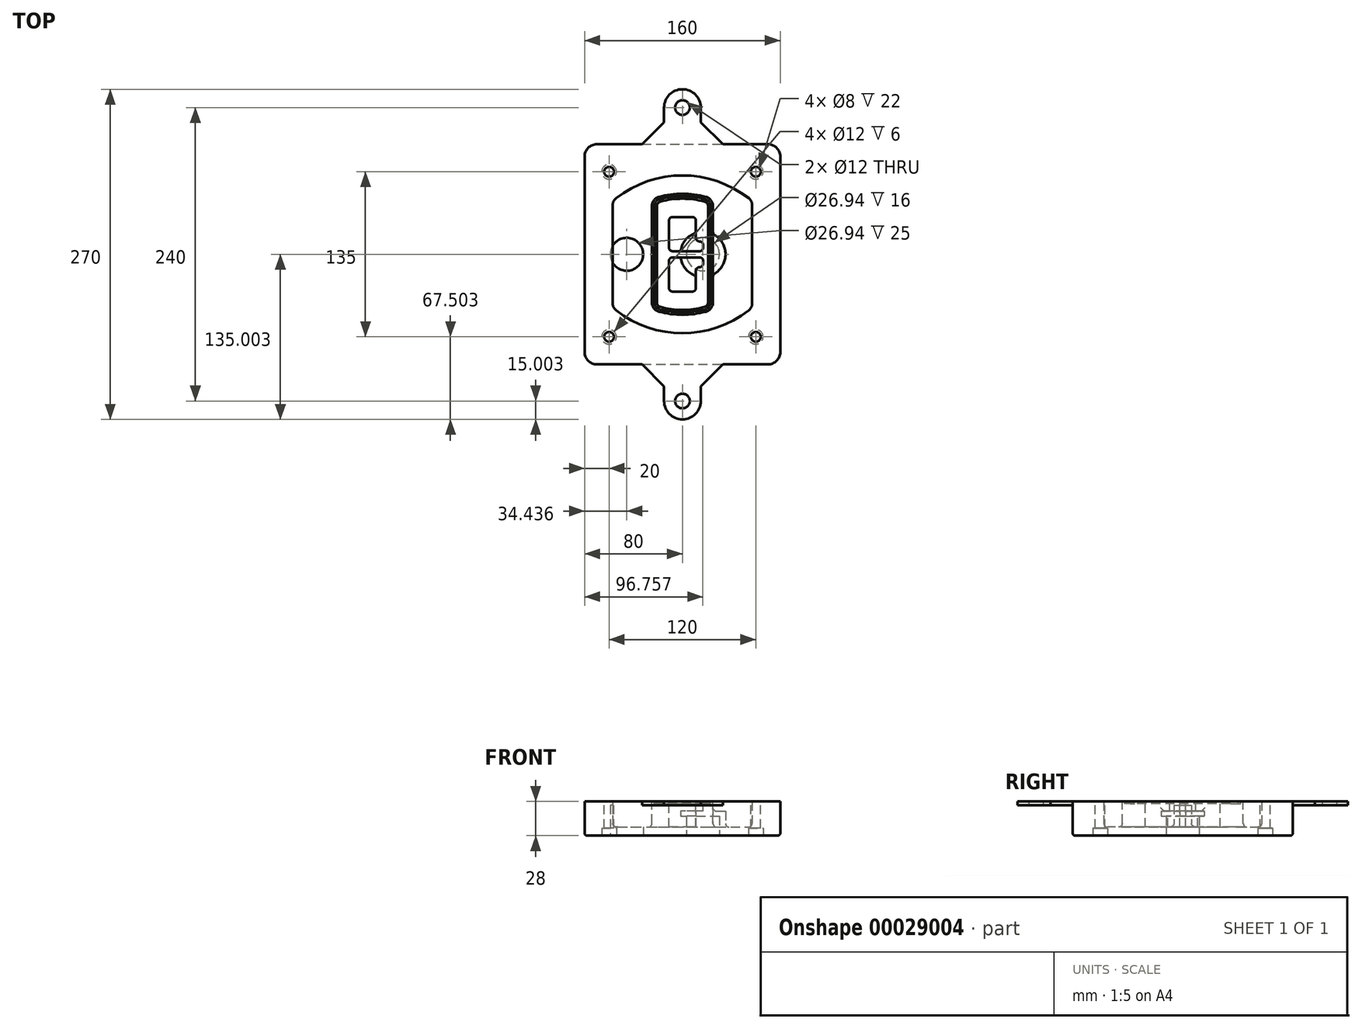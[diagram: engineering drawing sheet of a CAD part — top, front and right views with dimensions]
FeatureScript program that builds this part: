
annotation { "Feature Type Name" : "Feature", "Feature Type Description" : "" }
export const myFeature = defineFeature(function(context is Context, id is Id, definition is map)
    precondition{}
    {
        {
            var Q0;
            Q0=qCreatedBy(makeId("Top.planeOp"),FACE);
            var sketch = newSketch(context, id + "F0", { "sketchPlane" : qUnion([Q0])});
            skPoint(sketch, "E0.rect.middle", {"position": v(0, 0) * mm});
            skLineSegment(sketch, "E1.bottom", {"start": v(24.05, 28.38) * mm, "end": v(164.05, 28.38) * mm});
            skLineSegment(sketch, "E1.top", {"start": v(24.05, 208.38) * mm, "end": v(164.05, 208.38) * mm});
            skLineSegment(sketch, "E1.left", {"start": v(14.05, 38.38) * mm, "end": v(14.05, 198.38) * mm});
            skLineSegment(sketch, "E1.right", {"start": v(174.05, 38.38) * mm, "end": v(174.05, 198.38) * mm});
            skLineSegment(sketch, "E2", {"start": v(14.05, 208.38) * mm, "end": v(174.05, 28.38) * mm, "construction": true});
            skLineSegment(sketch, "E3", {"start": v(174.05, 208.38) * mm, "end": v(14.05, 28.38) * mm, "construction": true});
            skCircle(sketch, "E4", {"center": v(34.05, 185.88) * mm, "radius": 4 * mm});
            skCircle(sketch, "E5", {"center": v(154.05, 185.88) * mm, "radius": 4 * mm});
            skCircle(sketch, "E6", {"center": v(154.05, 50.88) * mm, "radius": 4 * mm});
            skCircle(sketch, "E7", {"center": v(34.05, 50.88) * mm, "radius": 4 * mm});
            skLineSegment(sketch, "E8", {"start": v(34.05, 185.88) * mm, "end": v(154.05, 185.88) * mm, "construction": true});
            skLineSegment(sketch, "E9", {"start": v(154.05, 185.88) * mm, "end": v(154.05, 50.88) * mm, "construction": true});
            skLineSegment(sketch, "E10", {"start": v(154.05, 50.88) * mm, "end": v(34.05, 50.88) * mm, "construction": true});
            skLineSegment(sketch, "E11", {"start": v(34.05, 50.88) * mm, "end": v(34.05, 185.88) * mm, "construction": true});
            skLineSegment(sketch, "E12", {"start": v(34.05, 158.68) * mm, "end": v(34.05, 78.09) * mm});
            skLineSegment(sketch, "E13", {"start": v(154.05, 158.68) * mm, "end": v(154.05, 78.09) * mm});
            skArc(sketch, "E14", {"start": v(150.2, 166.56) * mm, "mid": v(94.05, 185.88) * mm, "end": v(37.9, 166.56) * mm});
            skArc(sketch, "E15", {"start": v(37.9, 70.2) * mm, "mid": v(94.05, 50.88) * mm, "end": v(150.2, 70.2) * mm});
            skLineSegment(sketch, "E16", {"start": v(34.05, 118.38) * mm, "end": v(154.05, 118.38) * mm, "construction": true});
            skPoint(sketch, "E17.visualSharp", {"position": v(34.05, 73.38) * mm});
            skArc(sketch, "E17.filletArc", {"start": v(34.05, 78.09) * mm, "mid": v(35.06, 73.7) * mm, "end": v(37.9, 70.2) * mm});
            skPoint(sketch, "E18.visualSharp", {"position": v(34.05, 163.38) * mm});
            skArc(sketch, "E18.filletArc", {"start": v(37.9, 166.56) * mm, "mid": v(35.06, 163.06) * mm, "end": v(34.05, 158.68) * mm});
            skPoint(sketch, "E19.visualSharp", {"position": v(154.05, 163.38) * mm});
            skArc(sketch, "E19.filletArc", {"start": v(154.05, 158.68) * mm, "mid": v(153.04, 163.06) * mm, "end": v(150.2, 166.56) * mm});
            skPoint(sketch, "E20.visualSharp", {"position": v(154.05, 73.38) * mm});
            skArc(sketch, "E20.filletArc", {"start": v(150.2, 70.2) * mm, "mid": v(153.04, 73.7) * mm, "end": v(154.05, 78.09) * mm});
            skPoint(sketch, "E21.visualSharp", {"position": v(14.05, 208.38) * mm});
            skArc(sketch, "E21.filletArc", {"start": v(24.05, 208.38) * mm, "mid": v(16.98, 205.45) * mm, "end": v(14.05, 198.38) * mm});
            skPoint(sketch, "E22.visualSharp", {"position": v(174.05, 208.38) * mm});
            skArc(sketch, "E22.filletArc", {"start": v(174.05, 198.38) * mm, "mid": v(171.12, 205.45) * mm, "end": v(164.05, 208.38) * mm});
            skPoint(sketch, "E23.visualSharp", {"position": v(174.05, 28.38) * mm});
            skArc(sketch, "E23.filletArc", {"start": v(164.05, 28.38) * mm, "mid": v(171.12, 31.31) * mm, "end": v(174.05, 38.38) * mm});
            skPoint(sketch, "E24.visualSharp", {"position": v(14.05, 28.38) * mm});
            skArc(sketch, "E24.filletArc", {"start": v(14.05, 38.38) * mm, "mid": v(16.98, 31.31) * mm, "end": v(24.05, 28.38) * mm});
            skArc(sketch, "E25.0", {"start": v(151.05, 158.68) * mm, "mid": v(150.34, 161.75) * mm, "end": v(148.36, 164.2) * mm});
            skLineSegment(sketch, "E25.1", {"start": v(151.05, 158.68) * mm, "end": v(151.05, 78.09) * mm});
            skArc(sketch, "E25.2", {"start": v(148.36, 72.57) * mm, "mid": v(150.34, 75.02) * mm, "end": v(151.05, 78.09) * mm});
            skArc(sketch, "E25.3", {"start": v(39.74, 72.57) * mm, "mid": v(94.05, 53.88) * mm, "end": v(148.36, 72.57) * mm});
            skArc(sketch, "E25.4", {"start": v(37.05, 78.09) * mm, "mid": v(37.76, 75.02) * mm, "end": v(39.74, 72.57) * mm});
            skArc(sketch, "E25.5", {"start": v(148.36, 164.2) * mm, "mid": v(94.05, 182.88) * mm, "end": v(39.74, 164.2) * mm});
            skLineSegment(sketch, "E25.6", {"start": v(37.05, 158.68) * mm, "end": v(37.05, 78.09) * mm});
            skArc(sketch, "E25.7", {"start": v(39.74, 164.2) * mm, "mid": v(37.76, 161.75) * mm, "end": v(37.05, 158.68) * mm});
            skArc(sketch, "E26.0", {"start": v(35.43, 169.71) * mm, "mid": v(31.47, 164.82) * mm, "end": v(30.05, 158.68) * mm});
            skArc(sketch, "E26.1", {"start": v(152.67, 169.71) * mm, "mid": v(94.05, 189.88) * mm, "end": v(35.43, 169.71) * mm});
            skArc(sketch, "E26.2", {"start": v(158.05, 158.68) * mm, "mid": v(156.63, 164.82) * mm, "end": v(152.67, 169.71) * mm});
            skLineSegment(sketch, "E26.3", {"start": v(158.05, 158.68) * mm, "end": v(158.05, 78.09) * mm});
            skArc(sketch, "E26.4", {"start": v(152.67, 67.05) * mm, "mid": v(156.63, 71.95) * mm, "end": v(158.05, 78.09) * mm});
            skLineSegment(sketch, "E26.5", {"start": v(30.05, 158.68) * mm, "end": v(30.05, 78.09) * mm});
            skArc(sketch, "E26.6", {"start": v(35.43, 67.05) * mm, "mid": v(94.05, 46.88) * mm, "end": v(152.67, 67.05) * mm});
            skArc(sketch, "E26.7", {"start": v(30.05, 78.09) * mm, "mid": v(31.47, 71.95) * mm, "end": v(35.43, 67.05) * mm});
            skSolve(sketch);
        }
        {
            var Q0;
            Q0=makeQuery(id+"F0.imprint","IMPRINT",FACE,{"disambiguationData":[TD([[makeQuery(id+"F0.imprint","IMPRINT",EDGE,{"derivedFrom":sQuery(id+"F0.wireOp",EDGE,"E1.bottom")}),1.0]])]});
            var Q1;
            Q1=makeQuery(id+"F0.imprint","IMPRINT",FACE,{"disambiguationData":[TD([[makeQuery(id+"F0.imprint","IMPRINT",EDGE,{"derivedFrom":sQuery(id+"F0.wireOp",EDGE,"E12")}),1.0]])]});
            var Q2;
            Q2=makeQuery(id+"F0.imprint","IMPRINT",FACE,{"disambiguationData":[TD([[makeQuery(id+"F0.imprint","IMPRINT",EDGE,{"derivedFrom":sQuery(id+"F0.wireOp",EDGE,"E25.0")}),1.0]])]});
            var Q3;
            Q3=makeQuery(id+"F0.imprint","IMPRINT",FACE,{"disambiguationData":[TD([[makeQuery(id+"F0.imprint","IMPRINT",EDGE,{"derivedFrom":sQuery(id+"F0.wireOp",EDGE,"E12")}),-1.0]])]});
            extrude(context, id + "F1", {"entities" : qUnion([Q0, Q1, Q2, Q3]), "oppositeDirection" : true, "depth" : 25 * mm});
        }
        {
            var Q0;
            Q0=makeQuery(id+"F0.imprint","IMPRINT",FACE,{"disambiguationData":[TD([[makeQuery(id+"F0.imprint","IMPRINT",EDGE,{"derivedFrom":sQuery(id+"F0.wireOp",EDGE,"E12")}),1.0]])]});
            extrude(context, id + "F2", {"entities" : qUnion([Q0]), "operationType" : NewBodyOperationType.ADD, "depth" : 3 * mm});
        }
        {
            var Q0;
            Q0=makeQuery(id+"F0.imprint","IMPRINT",FACE,{"disambiguationData":[TD([[makeQuery(id+"F0.imprint","IMPRINT",EDGE,{"derivedFrom":sQuery(id+"F0.wireOp",EDGE,"E25.0")}),1.0]])]});
            extrude(context, id + "F3", {"entities" : qUnion([Q0]), "operationType" : NewBodyOperationType.REMOVE, "oppositeDirection" : true, "depth" : 18 * mm});
        }
        {
            var Q0;
            Q0=makeQuery(id+"F2.opExtrude","CAP_FACE",FACE,{"disambiguationData":[OSD([sQuery(id+"F0.wireOp",EDGE,"E12"),sQuery(id+"F0.wireOp",EDGE,"E13"),sQuery(id+"F0.wireOp",EDGE,"E14"),sQuery(id+"F0.wireOp",EDGE,"E15"),sQuery(id+"F0.wireOp",EDGE,"E17.filletArc"),sQuery(id+"F0.wireOp",EDGE,"E18.filletArc"),sQuery(id+"F0.wireOp",EDGE,"E19.filletArc"),sQuery(id+"F0.wireOp",EDGE,"E20.filletArc"),sQuery(id+"F0.wireOp",EDGE,"E25.0"),sQuery(id+"F0.wireOp",EDGE,"E25.1"),sQuery(id+"F0.wireOp",EDGE,"E25.2"),sQuery(id+"F0.wireOp",EDGE,"E25.3"),sQuery(id+"F0.wireOp",EDGE,"E25.4"),sQuery(id+"F0.wireOp",EDGE,"E25.5"),sQuery(id+"F0.wireOp",EDGE,"E25.6"),sQuery(id+"F0.wireOp",EDGE,"E25.7")])],"isStart":false});
            var sketch = newSketch(context, id + "F4", { "sketchPlane" : qUnion([Q0])});
            skArc(sketch, "E27.0", {"start": v(74.97, 71.41) * mm, "mid": v(94.05, 68.88) * mm, "end": v(113.13, 71.41) * mm});
            skArc(sketch, "E28.0", {"start": v(113.13, 165.35) * mm, "mid": v(94.05, 167.88) * mm, "end": v(74.97, 165.35) * mm});
            skLineSegment(sketch, "E29", {"start": v(69.05, 157.63) * mm, "end": v(69.05, 79.14) * mm});
            skLineSegment(sketch, "E30", {"start": v(119.05, 157.63) * mm, "end": v(119.05, 79.14) * mm});
            skLineSegment(sketch, "E31", {"start": v(69.05, 163.48) * mm, "end": v(119.05, 163.48) * mm, "construction": true});
            skLineSegment(sketch, "E32", {"start": v(69.05, 73.28) * mm, "end": v(119.05, 73.28) * mm, "construction": true});
            skPoint(sketch, "E33.visualSharp", {"position": v(69.05, 163.48) * mm});
            skArc(sketch, "E33.filletArc", {"start": v(74.97, 165.35) * mm, "mid": v(70.7, 162.5) * mm, "end": v(69.05, 157.63) * mm});
            skPoint(sketch, "E34.visualSharp", {"position": v(119.05, 163.48) * mm});
            skArc(sketch, "E34.filletArc", {"start": v(119.05, 157.63) * mm, "mid": v(117.4, 162.5) * mm, "end": v(113.13, 165.35) * mm});
            skPoint(sketch, "E35.visualSharp", {"position": v(119.05, 73.28) * mm});
            skArc(sketch, "E35.filletArc", {"start": v(113.13, 71.41) * mm, "mid": v(117.4, 74.27) * mm, "end": v(119.05, 79.14) * mm});
            skPoint(sketch, "E36.visualSharp", {"position": v(69.05, 73.28) * mm});
            skArc(sketch, "E36.filletArc", {"start": v(69.05, 79.14) * mm, "mid": v(70.7, 74.27) * mm, "end": v(74.97, 71.41) * mm});
            skArc(sketch, "E37.0", {"start": v(148.36, 164.2) * mm, "mid": v(94.05, 182.88) * mm, "end": v(39.74, 164.2) * mm});
            skArc(sketch, "E37.1", {"start": v(39.74, 164.2) * mm, "mid": v(37.76, 161.75) * mm, "end": v(37.05, 158.68) * mm});
            skLineSegment(sketch, "E37.2", {"start": v(37.05, 158.68) * mm, "end": v(37.05, 78.09) * mm});
            skArc(sketch, "E37.3", {"start": v(37.05, 78.09) * mm, "mid": v(37.76, 75.02) * mm, "end": v(39.74, 72.57) * mm});
            skArc(sketch, "E37.4", {"start": v(39.74, 72.57) * mm, "mid": v(94.05, 53.88) * mm, "end": v(148.36, 72.57) * mm});
            skArc(sketch, "E37.5", {"start": v(148.36, 72.57) * mm, "mid": v(150.34, 75.02) * mm, "end": v(151.05, 78.09) * mm});
            skLineSegment(sketch, "E37.6", {"start": v(151.05, 158.68) * mm, "end": v(151.05, 78.09) * mm});
            skArc(sketch, "E37.7", {"start": v(151.05, 158.68) * mm, "mid": v(150.34, 161.75) * mm, "end": v(148.36, 164.2) * mm});
            skLineSegment(sketch, "E38.0", {"start": v(117.05, 157.63) * mm, "end": v(117.05, 79.14) * mm});
            skArc(sketch, "E38.1", {"start": v(112.61, 73.34) * mm, "mid": v(115.81, 75.49) * mm, "end": v(117.05, 79.14) * mm});
            skArc(sketch, "E38.2", {"start": v(75.49, 73.34) * mm, "mid": v(94.05, 70.88) * mm, "end": v(112.61, 73.34) * mm});
            skArc(sketch, "E38.3", {"start": v(71.05, 79.14) * mm, "mid": v(72.29, 75.49) * mm, "end": v(75.49, 73.34) * mm});
            skLineSegment(sketch, "E38.4", {"start": v(71.05, 157.63) * mm, "end": v(71.05, 79.14) * mm});
            skArc(sketch, "E38.5", {"start": v(117.05, 157.63) * mm, "mid": v(115.81, 161.28) * mm, "end": v(112.61, 163.42) * mm});
            skArc(sketch, "E38.6", {"start": v(75.49, 163.42) * mm, "mid": v(72.29, 161.28) * mm, "end": v(71.05, 157.63) * mm});
            skArc(sketch, "E38.7", {"start": v(112.61, 163.42) * mm, "mid": v(94.05, 165.88) * mm, "end": v(75.49, 163.42) * mm});
            skArc(sketch, "E39.0", {"start": v(115.05, 157.63) * mm, "mid": v(114.23, 160.06) * mm, "end": v(112.1, 161.5) * mm});
            skLineSegment(sketch, "E39.1", {"start": v(115.05, 157.63) * mm, "end": v(115.05, 79.14) * mm});
            skArc(sketch, "E39.2", {"start": v(112.1, 75.27) * mm, "mid": v(114.23, 76.7) * mm, "end": v(115.05, 79.14) * mm});
            skArc(sketch, "E39.3", {"start": v(76, 75.27) * mm, "mid": v(94.05, 72.88) * mm, "end": v(112.1, 75.27) * mm});
            skArc(sketch, "E39.4", {"start": v(73.05, 79.14) * mm, "mid": v(73.87, 76.7) * mm, "end": v(76, 75.27) * mm});
            skArc(sketch, "E39.5", {"start": v(112.1, 161.5) * mm, "mid": v(94.05, 163.88) * mm, "end": v(76, 161.5) * mm});
            skLineSegment(sketch, "E39.6", {"start": v(73.05, 157.63) * mm, "end": v(73.05, 79.14) * mm});
            skArc(sketch, "E39.7", {"start": v(76, 161.5) * mm, "mid": v(73.87, 160.06) * mm, "end": v(73.05, 157.63) * mm});
            skLineSegment(sketch, "E40", {"start": v(69.05, 118.38) * mm, "end": v(119.05, 118.38) * mm, "construction": true});
            skLineSegment(sketch, "E41", {"start": v(83.05, 123.88) * mm, "end": v(83.05, 145.88) * mm});
            skLineSegment(sketch, "E42", {"start": v(86.05, 148.88) * mm, "end": v(102.05, 148.88) * mm});
            skLineSegment(sketch, "E43", {"start": v(105.05, 145.88) * mm, "end": v(105.05, 131.88) * mm});
            skLineSegment(sketch, "E44", {"start": v(108.05, 128.88) * mm, "end": v(108.05, 128.88) * mm});
            skLineSegment(sketch, "E45", {"start": v(111.05, 125.88) * mm, "end": v(111.05, 123.88) * mm});
            skLineSegment(sketch, "E46", {"start": v(108.05, 120.88) * mm, "end": v(86.05, 120.88) * mm});
            skPoint(sketch, "E47.visualSharp", {"position": v(83.05, 148.88) * mm});
            skArc(sketch, "E47.filletArc", {"start": v(86.05, 148.88) * mm, "mid": v(83.93, 148) * mm, "end": v(83.05, 145.88) * mm});
            skPoint(sketch, "E48.visualSharp", {"position": v(105.05, 148.88) * mm});
            skArc(sketch, "E48.filletArc", {"start": v(105.05, 145.88) * mm, "mid": v(104.17, 148) * mm, "end": v(102.05, 148.88) * mm});
            skPoint(sketch, "E49.visualSharp", {"position": v(105.05, 128.88) * mm});
            skArc(sketch, "E49.filletArc", {"start": v(105.05, 131.88) * mm, "mid": v(105.93, 129.76) * mm, "end": v(108.05, 128.88) * mm});
            skPoint(sketch, "E50.visualSharp", {"position": v(111.05, 128.88) * mm});
            skArc(sketch, "E50.filletArc", {"start": v(111.05, 125.88) * mm, "mid": v(110.17, 128) * mm, "end": v(108.05, 128.88) * mm});
            skPoint(sketch, "E51.visualSharp", {"position": v(111.05, 120.88) * mm});
            skArc(sketch, "E51.filletArc", {"start": v(108.05, 120.88) * mm, "mid": v(110.17, 121.76) * mm, "end": v(111.05, 123.88) * mm});
            skPoint(sketch, "E52.visualSharp", {"position": v(83.05, 120.88) * mm});
            skArc(sketch, "E52.filletArc", {"start": v(83.05, 123.88) * mm, "mid": v(83.93, 121.76) * mm, "end": v(86.05, 120.88) * mm});
            skLineSegment(sketch, "E53.0.MirrorCS", {"start": v(108.05, 115.88) * mm, "end": v(86.05, 115.88) * mm});
            skArc(sketch, "E54.0.MirrorCS", {"start": v(83.05, 112.88) * mm, "mid": v(83.93, 115) * mm, "end": v(86.05, 115.88) * mm});
            skLineSegment(sketch, "E55.0.MirrorCS", {"start": v(83.05, 112.88) * mm, "end": v(83.05, 90.88) * mm});
            skArc(sketch, "E56.0.MirrorCS", {"start": v(86.05, 87.88) * mm, "mid": v(83.93, 88.76) * mm, "end": v(83.05, 90.88) * mm});
            skLineSegment(sketch, "E57.0.MirrorCS", {"start": v(86.05, 87.88) * mm, "end": v(102.05, 87.88) * mm});
            skArc(sketch, "E58.0.MirrorCS", {"start": v(105.05, 90.88) * mm, "mid": v(104.17, 88.76) * mm, "end": v(102.05, 87.88) * mm});
            skLineSegment(sketch, "E59.0.MirrorCS", {"start": v(105.05, 90.88) * mm, "end": v(105.05, 104.88) * mm});
            skArc(sketch, "E60.0.MirrorCS", {"start": v(105.05, 104.88) * mm, "mid": v(105.93, 107) * mm, "end": v(108.05, 107.88) * mm});
            skArc(sketch, "E61.0.MirrorCS", {"start": v(111.05, 110.88) * mm, "mid": v(110.17, 108.76) * mm, "end": v(108.05, 107.88) * mm});
            skLineSegment(sketch, "E62.0.MirrorCS", {"start": v(111.05, 110.88) * mm, "end": v(111.05, 112.88) * mm});
            skArc(sketch, "E63.0.MirrorCS", {"start": v(108.05, 115.88) * mm, "mid": v(110.17, 115) * mm, "end": v(111.05, 112.88) * mm});
            skSolve(sketch);
        }
        {
            var Q0;
            Q0=makeQuery(id+"F4.imprint","IMPRINT",FACE,{"disambiguationData":[TD([[makeQuery(id+"F4.imprint","IMPRINT",EDGE,{"derivedFrom":sQuery(id+"F4.wireOp",EDGE,"E27.0")}),1.0]])]});
            var Q1;
            Q1=makeQuery(id+"F4.imprint","IMPRINT",FACE,{"disambiguationData":[TD([[makeQuery(id+"F4.imprint","IMPRINT",EDGE,{"derivedFrom":sQuery(id+"F4.wireOp",EDGE,"E38.0")}),-1.0]])]});
            var Q2;
            Q2=makeQuery(id+"F4.imprint","IMPRINT",FACE,{"disambiguationData":[TD([[makeQuery(id+"F4.imprint","IMPRINT",EDGE,{"derivedFrom":sQuery(id+"F4.wireOp",EDGE,"E39.0")}),1.0]])]});
            extrude(context, id + "F5", {"entities" : qUnion([Q0, Q1, Q2]), "operationType" : NewBodyOperationType.ADD, "endBound" : BoundingType.UP_TO_NEXT, "oppositeDirection" : true, "depth" : 25 * mm});
        }
        {
            var Q0;
            Q0=makeQuery(id+"F4.imprint","IMPRINT",FACE,{"disambiguationData":[TD([[makeQuery(id+"F4.imprint","IMPRINT",EDGE,{"derivedFrom":sQuery(id+"F4.wireOp",EDGE,"E38.0")}),-1.0]])]});
            extrude(context, id + "F6", {"entities" : qUnion([Q0]), "operationType" : NewBodyOperationType.REMOVE, "oppositeDirection" : true, "depth" : 2 * mm});
        }
        {
            var Q0;
            Q0=makeQuery(id+"F1.opExtrude","CAP_FACE",FACE,{"disambiguationData":[OSD([sQuery(id+"F0.wireOp",EDGE,"E1.bottom"),sQuery(id+"F0.wireOp",EDGE,"E1.top"),sQuery(id+"F0.wireOp",EDGE,"E1.left"),sQuery(id+"F0.wireOp",EDGE,"E1.right"),sQuery(id+"F0.wireOp",EDGE,"E4"),sQuery(id+"F0.wireOp",EDGE,"E5"),sQuery(id+"F0.wireOp",EDGE,"E6"),sQuery(id+"F0.wireOp",EDGE,"E7"),sQuery(id+"F0.wireOp",EDGE,"E21.filletArc"),sQuery(id+"F0.wireOp",EDGE,"E22.filletArc"),sQuery(id+"F0.wireOp",EDGE,"E23.filletArc"),sQuery(id+"F0.wireOp",EDGE,"E24.filletArc")])],"isStart":false});
            var sketch = newSketch(context, id + "F7", { "sketchPlane" : qUnion([Q0])});
            skCircle(sketch, "E64", {"center": v(110.8, -118.38) * mm, "radius": 13.47 * mm});
            skCircle(sketch, "E65", {"center": v(48.49, -118.38) * mm, "radius": 13.47 * mm});
            skLineSegment(sketch, "E66", {"start": v(174.05, -118.38) * mm, "end": v(14.05, -118.38) * mm});
            skCircle(sketch, "E67", {"center": v(110.8, -118.38) * mm, "radius": 18.47 * mm});
            skCircle(sketch, "E68", {"center": v(154.05, -185.88) * mm, "radius": 6 * mm});
            skCircle(sketch, "E69", {"center": v(34.05, -185.88) * mm, "radius": 6 * mm});
            skCircle(sketch, "E70", {"center": v(34.05, -50.88) * mm, "radius": 6 * mm});
            skCircle(sketch, "E71", {"center": v(154.05, -50.88) * mm, "radius": 6 * mm});
            skSolve(sketch);
        }
        {
            var Q0;
            {var subQ1=sQuery(id+"F7.wireOp",EDGE,"E66");var subQ4=sQuery(id+"F7.wireOp",EDGE,"E64");var subQ6=makeQuery(id+"F7.imprint","INTERSECT",VERTEX,{"disambiguationData":[OD(0.0)],"derivedFrom":[subQ4,subQ1]});Q0=makeQuery(id+"F7.imprint","IMPRINT",FACE,{"disambiguationData":[TD([[makeQuery(id+"F7.imprint","IMPRINT",EDGE,{"disambiguationData":[TD([[subQ6,-1.0]])],"derivedFrom":subQ4}),-1.0]])]});}
            var Q1;
            {var subQ0=sQuery(id+"F7.wireOp",EDGE,"E66");var subQ1=sQuery(id+"F7.wireOp",EDGE,"E64");var subQ3=makeQuery(id+"F7.imprint","INTERSECT",VERTEX,{"disambiguationData":[OD(0.0)],"derivedFrom":[subQ1,subQ0]});Q1=makeQuery(id+"F7.imprint","IMPRINT",FACE,{"disambiguationData":[TD([[makeQuery(id+"F7.imprint","IMPRINT",EDGE,{"disambiguationData":[TD([[subQ3,-1.0]])],"derivedFrom":subQ1}),1.0]])]});}
            var Q2;
            {var subQ0=sQuery(id+"F7.wireOp",EDGE,"E66");var subQ1=sQuery(id+"F7.wireOp",EDGE,"E64");var subQ3=makeQuery(id+"F7.imprint","INTERSECT",VERTEX,{"disambiguationData":[OD(0.0)],"derivedFrom":[subQ1,subQ0]});Q2=makeQuery(id+"F7.imprint","IMPRINT",FACE,{"disambiguationData":[TD([[makeQuery(id+"F7.imprint","IMPRINT",EDGE,{"disambiguationData":[TD([[subQ3,1.0]])],"derivedFrom":subQ1}),1.0]])]});}
            var Q3;
            {var subQ1=sQuery(id+"F7.wireOp",EDGE,"E66");var subQ4=sQuery(id+"F7.wireOp",EDGE,"E64");var subQ6=makeQuery(id+"F7.imprint","INTERSECT",VERTEX,{"disambiguationData":[OD(0.0)],"derivedFrom":[subQ4,subQ1]});Q3=makeQuery(id+"F7.imprint","IMPRINT",FACE,{"disambiguationData":[TD([[makeQuery(id+"F7.imprint","IMPRINT",EDGE,{"disambiguationData":[TD([[subQ6,1.0]])],"derivedFrom":subQ4}),-1.0]])]});}
            extrude(context, id + "F8", {"entities" : qUnion([Q0, Q1, Q2, Q3]), "operationType" : NewBodyOperationType.ADD, "oppositeDirection" : true, "depth" : 20 * mm});
        }
        {
            var Q0;
            {var subQ0=sQuery(id+"F7.wireOp",EDGE,"E66");var subQ1=sQuery(id+"F7.wireOp",EDGE,"E64");var subQ3=makeQuery(id+"F7.imprint","INTERSECT",VERTEX,{"disambiguationData":[OD(0.0)],"derivedFrom":[subQ1,subQ0]});Q0=makeQuery(id+"F7.imprint","IMPRINT",FACE,{"disambiguationData":[TD([[makeQuery(id+"F7.imprint","IMPRINT",EDGE,{"disambiguationData":[TD([[subQ3,-1.0]])],"derivedFrom":subQ1}),1.0]])]});}
            var Q1;
            {var subQ0=sQuery(id+"F7.wireOp",EDGE,"E66");var subQ1=sQuery(id+"F7.wireOp",EDGE,"E64");var subQ3=makeQuery(id+"F7.imprint","INTERSECT",VERTEX,{"disambiguationData":[OD(0.0)],"derivedFrom":[subQ1,subQ0]});Q1=makeQuery(id+"F7.imprint","IMPRINT",FACE,{"disambiguationData":[TD([[makeQuery(id+"F7.imprint","IMPRINT",EDGE,{"disambiguationData":[TD([[subQ3,1.0]])],"derivedFrom":subQ1}),1.0]])]});}
            extrude(context, id + "F9", {"entities" : qUnion([Q0, Q1]), "operationType" : NewBodyOperationType.REMOVE, "oppositeDirection" : true, "depth" : 16 * mm});
        }
        {
            var Q0;
            {var subQ0=sQuery(id+"F7.wireOp",EDGE,"E66");var subQ1=sQuery(id+"F7.wireOp",EDGE,"E65");var subQ3=makeQuery(id+"F7.imprint","INTERSECT",VERTEX,{"disambiguationData":[OD(0.0)],"derivedFrom":[subQ1,subQ0]});Q0=makeQuery(id+"F7.imprint","IMPRINT",FACE,{"disambiguationData":[TD([[makeQuery(id+"F7.imprint","IMPRINT",EDGE,{"disambiguationData":[TD([[subQ3,-1.0]])],"derivedFrom":subQ1}),1.0]])]});}
            var Q1;
            {var subQ0=sQuery(id+"F7.wireOp",EDGE,"E66");var subQ1=sQuery(id+"F7.wireOp",EDGE,"E65");var subQ3=makeQuery(id+"F7.imprint","INTERSECT",VERTEX,{"disambiguationData":[OD(0.0)],"derivedFrom":[subQ1,subQ0]});Q1=makeQuery(id+"F7.imprint","IMPRINT",FACE,{"disambiguationData":[TD([[makeQuery(id+"F7.imprint","IMPRINT",EDGE,{"disambiguationData":[TD([[subQ3,1.0]])],"derivedFrom":subQ1}),1.0]])]});}
            extrude(context, id + "F10", {"entities" : qUnion([Q0, Q1]), "operationType" : NewBodyOperationType.REMOVE, "oppositeDirection" : true, "depth" : 25 * mm});
        }
        {
            var Q0;
            Q0=makeQuery(id+"F7.imprint","IMPRINT",FACE,{"disambiguationData":[TD([[makeQuery(id+"F7.imprint","IMPRINT",EDGE,{"derivedFrom":sQuery(id+"F7.wireOp",EDGE,"E68")}),1.0]])]});
            var Q1;
            Q1=makeQuery(id+"F7.imprint","IMPRINT",FACE,{"disambiguationData":[TD([[makeQuery(id+"F7.imprint","IMPRINT",EDGE,{"derivedFrom":makeQuery(id+"F1.opExtrude","CAP_EDGE",EDGE,{"disambiguationData":[OSD([sQuery(id+"F0.wireOp",EDGE,"E5")])],"isStart":false})}),-1.0]])]});
            var Q2;
            Q2=makeQuery(id+"F7.imprint","IMPRINT",FACE,{"disambiguationData":[TD([[makeQuery(id+"F7.imprint","IMPRINT",EDGE,{"derivedFrom":sQuery(id+"F7.wireOp",EDGE,"E69")}),1.0]])]});
            var Q3;
            Q3=makeQuery(id+"F7.imprint","IMPRINT",FACE,{"disambiguationData":[TD([[makeQuery(id+"F7.imprint","IMPRINT",EDGE,{"derivedFrom":makeQuery(id+"F1.opExtrude","CAP_EDGE",EDGE,{"disambiguationData":[OSD([sQuery(id+"F0.wireOp",EDGE,"E4")])],"isStart":false})}),-1.0]])]});
            var Q4;
            Q4=makeQuery(id+"F7.imprint","IMPRINT",FACE,{"disambiguationData":[TD([[makeQuery(id+"F7.imprint","IMPRINT",EDGE,{"derivedFrom":sQuery(id+"F7.wireOp",EDGE,"E70")}),1.0]])]});
            var Q5;
            Q5=makeQuery(id+"F7.imprint","IMPRINT",FACE,{"disambiguationData":[TD([[makeQuery(id+"F7.imprint","IMPRINT",EDGE,{"derivedFrom":makeQuery(id+"F1.opExtrude","CAP_EDGE",EDGE,{"disambiguationData":[OSD([sQuery(id+"F0.wireOp",EDGE,"E7")])],"isStart":false})}),-1.0]])]});
            var Q6;
            Q6=makeQuery(id+"F7.imprint","IMPRINT",FACE,{"disambiguationData":[TD([[makeQuery(id+"F7.imprint","IMPRINT",EDGE,{"derivedFrom":sQuery(id+"F7.wireOp",EDGE,"E71")}),1.0]])]});
            var Q7;
            Q7=makeQuery(id+"F7.imprint","IMPRINT",FACE,{"disambiguationData":[TD([[makeQuery(id+"F7.imprint","IMPRINT",EDGE,{"derivedFrom":makeQuery(id+"F1.opExtrude","CAP_EDGE",EDGE,{"disambiguationData":[OSD([sQuery(id+"F0.wireOp",EDGE,"E6")])],"isStart":false})}),-1.0]])]});
            extrude(context, id + "F11", {"entities" : qUnion([Q0, Q1, Q2, Q3, Q4, Q5, Q6, Q7]), "operationType" : NewBodyOperationType.REMOVE, "oppositeDirection" : true, "depth" : 6 * mm});
        }
        {
            var Q0;
            Q0=makeQuery(id+"F9.boolean.opBoolean","COPY",FACE,{"derivedFrom":makeQuery(id+"F9.opExtrude","CAP_FACE",FACE,{"disambiguationData":[OSD([sQuery(id+"F7.wireOp",EDGE,"E64")])],"isStart":false})});
            var sketch = newSketch(context, id + "F12", { "sketchPlane" : qUnion([Q0])});
            skArc(sketch, "E72.0", {"start": v(105.05, -100.83) * mm, "mid": v(96.62, -106.56) * mm, "end": v(92.5, -115.88) * mm});
            skArc(sketch, "E72.1", {"start": v(92.5, -120.88) * mm, "mid": v(96.62, -130.2) * mm, "end": v(105.05, -135.93) * mm});
            skLineSegment(sketch, "E73", {"start": v(92.5, -120.88) * mm, "end": v(108.05, -120.88) * mm});
            skLineSegment(sketch, "E74.0", {"start": v(108.05, -115.88) * mm, "end": v(92.5, -115.88) * mm});
            skArc(sketch, "E74.1", {"start": v(108.05, -115.88) * mm, "mid": v(110.17, -115) * mm, "end": v(111.05, -112.88) * mm});
            skLineSegment(sketch, "E74.2", {"start": v(111.05, -110.88) * mm, "end": v(111.05, -112.88) * mm});
            skArc(sketch, "E74.3", {"start": v(111.05, -110.88) * mm, "mid": v(110.17, -108.76) * mm, "end": v(108.05, -107.88) * mm});
            skArc(sketch, "E74.4", {"start": v(105.05, -104.88) * mm, "mid": v(105.93, -107) * mm, "end": v(108.05, -107.88) * mm});
            skLineSegment(sketch, "E74.5", {"start": v(105.05, -100.83) * mm, "end": v(105.05, -104.88) * mm});
            skLineSegment(sketch, "E74.7", {"start": v(108.05, -120.88) * mm, "end": v(92.5, -120.88) * mm});
            skArc(sketch, "E74.8", {"start": v(108.05, -120.88) * mm, "mid": v(110.17, -121.76) * mm, "end": v(111.05, -123.88) * mm});
            skLineSegment(sketch, "E74.9", {"start": v(111.05, -125.88) * mm, "end": v(111.05, -123.88) * mm});
            skArc(sketch, "E74.10", {"start": v(111.05, -125.88) * mm, "mid": v(110.17, -128) * mm, "end": v(108.05, -128.88) * mm});
            skArc(sketch, "E74.11", {"start": v(105.05, -131.88) * mm, "mid": v(105.93, -129.76) * mm, "end": v(108.05, -128.88) * mm});
            skLineSegment(sketch, "E74.12", {"start": v(105.05, -135.93) * mm, "end": v(105.05, -131.88) * mm});
            skPoint(sketch, "E75.orphan", {"position": v(105.05, -145.88) * mm});
            skPoint(sketch, "E76.orphan", {"position": v(86.05, -120.88) * mm});
            skPoint(sketch, "E77.orphan", {"position": v(86.05, -115.88) * mm});
            skPoint(sketch, "E78.orphan", {"position": v(105.05, -90.88) * mm});
            skSolve(sketch);
        }
        {
            var Q0;
            {var subQ7=sQuery(id+"F12.wireOp",EDGE,"E72.0");var subQ14=sQuery(id+"F12.wireOp",EDGE,"E72.1");var subQ16=sQuery(id+"F12.wireOp",EDGE,"E74.1");var subQ18=sQuery(id+"F12.wireOp",EDGE,"E74.8");Q0=qUnion([makeQuery(id+"F12.imprint","IMPRINT",FACE,{"disambiguationData":[TD([[makeQuery(id+"F12.imprint","IMPRINT",EDGE,{"derivedFrom":subQ7}),1.0]])]}),makeQuery(id+"F12.imprint","IMPRINT",FACE,{"disambiguationData":[TD([[makeQuery(id+"F12.imprint","IMPRINT",EDGE,{"derivedFrom":subQ14}),1.0]])]}),makeQuery(id+"F12.imprint","IMPRINT",FACE,{"disambiguationData":[TD([[makeQuery(id+"F12.imprint","IMPRINT",EDGE,{"derivedFrom":subQ16}),1.0]])]}),makeQuery(id+"F12.imprint","IMPRINT",FACE,{"disambiguationData":[TD([[makeQuery(id+"F12.imprint","IMPRINT",EDGE,{"derivedFrom":subQ18}),-1.0]])]})]);}
            var Q1;
            Q1=makeQuery(id+"F5.boolean.opBoolean","SPLIT",FACE,{"disambiguationData":[TD([makeQuery(id+"F5.opExtrude","SWEPT_FACE",FACE,{"disambiguationData":[OSD([sQuery(id+"F4.wireOp",EDGE,"E41")])]})])],"derivedFrom":makeQuery(id+"F3.boolean.opBoolean","COPY",FACE,{"derivedFrom":makeQuery(id+"F3.opExtrude","CAP_FACE",FACE,{"disambiguationData":[OSD([sQuery(id+"F0.wireOp",EDGE,"E25.0"),sQuery(id+"F0.wireOp",EDGE,"E25.1"),sQuery(id+"F0.wireOp",EDGE,"E25.2"),sQuery(id+"F0.wireOp",EDGE,"E25.3"),sQuery(id+"F0.wireOp",EDGE,"E25.4"),sQuery(id+"F0.wireOp",EDGE,"E25.5"),sQuery(id+"F0.wireOp",EDGE,"E25.6"),sQuery(id+"F0.wireOp",EDGE,"E25.7")])],"isStart":false})})});
            extrude(context, id + "F13", {"entities" : qUnion([Q0]), "operationType" : NewBodyOperationType.REMOVE, "endBound" : BoundingType.UP_TO_SURFACE, "endBoundEntityFace" : qUnion([Q1]), "depth" : 25 * mm});
        }
        {
            var Q0;
            Q0=makeQuery(id+"F3.boolean.opBoolean","COPY",EDGE,{"derivedFrom":makeQuery(id+"F3.opExtrude","CAP_EDGE",EDGE,{"disambiguationData":[OSD([sQuery(id+"F0.wireOp",EDGE,"E25.6")])],"isStart":false})});
            var Q1;
            Q1=makeQuery(id+"F8.boolean.opBoolean","INTERSECT",EDGE,{"derivedFrom":[makeQuery(id+"F5.opExtrude","SWEPT_FACE",FACE,{"disambiguationData":[OSD([sQuery(id+"F4.wireOp",EDGE,"E30")])]}),makeQuery(id+"F8.opExtrude","CAP_FACE",FACE,{"disambiguationData":[OSD([sQuery(id+"F7.wireOp",EDGE,"E67")])],"isStart":false})]});
            var Q2;
            Q2=makeQuery(id+"F8.boolean.opBoolean","INTERSECT",EDGE,{"disambiguationData":[OD(1.0)],"derivedFrom":[makeQuery(id+"F5.opExtrude","SWEPT_FACE",FACE,{"disambiguationData":[OSD([sQuery(id+"F4.wireOp",EDGE,"E30")])]}),makeQuery(id+"F8.opExtrude","SWEPT_FACE",FACE,{"disambiguationData":[OSD([sQuery(id+"F7.wireOp",EDGE,"E67")])]})]});
            var Q3;
            {var subQ0=sQuery(id+"F4.wireOp",EDGE,"E30");Q3=makeQuery(id+"F8.boolean.opBoolean","SPLIT",EDGE,{"disambiguationData":[TD([makeQuery(id+"F5.opExtrude","SWEPT_FACE",FACE,{"disambiguationData":[OSD([sQuery(id+"F4.wireOp",EDGE,"E35.filletArc")])]})])],"derivedFrom":makeQuery(id+"F5.opExtrude","CAP_EDGE",EDGE,{"disambiguationData":[OSD([subQ0])],"isStart":false})});}
            var Q4;
            {var subQ0=sQuery(id+"F0.wireOp",EDGE,"E25.7");var subQ1=sQuery(id+"F0.wireOp",EDGE,"E25.1");var subQ2=sQuery(id+"F0.wireOp",EDGE,"E25.6");var subQ3=sQuery(id+"F0.wireOp",EDGE,"E25.5");var subQ4=sQuery(id+"F0.wireOp",EDGE,"E25.4");var subQ5=sQuery(id+"F0.wireOp",EDGE,"E25.0");var subQ6=sQuery(id+"F0.wireOp",EDGE,"E25.2");var subQ7=sQuery(id+"F0.wireOp",EDGE,"E25.3");Q4=makeQuery(id+"F8.boolean.opBoolean","INTERSECT",EDGE,{"derivedFrom":[makeQuery(id+"F5.boolean.opBoolean","SPLIT",FACE,{"disambiguationData":[TD([makeQuery(id+"F2.opExtrude","SWEPT_FACE",FACE,{"disambiguationData":[OSD([subQ5])]})])],"derivedFrom":makeQuery(id+"F3.boolean.opBoolean","COPY",FACE,{"derivedFrom":makeQuery(id+"F3.opExtrude","CAP_FACE",FACE,{"disambiguationData":[OSD([subQ5,subQ1,subQ6,subQ7,subQ4,subQ3,subQ2,subQ0])],"isStart":false})})}),makeQuery(id+"F8.opExtrude","SWEPT_FACE",FACE,{"disambiguationData":[OSD([sQuery(id+"F7.wireOp",EDGE,"E67")])]})]});}
            var Q5;
            Q5=makeQuery(id+"F8.boolean.opBoolean","INTERSECT",EDGE,{"disambiguationData":[OD(0.0)],"derivedFrom":[makeQuery(id+"F5.opExtrude","SWEPT_FACE",FACE,{"disambiguationData":[OSD([sQuery(id+"F4.wireOp",EDGE,"E30")])]}),makeQuery(id+"F8.opExtrude","SWEPT_FACE",FACE,{"disambiguationData":[OSD([sQuery(id+"F7.wireOp",EDGE,"E67")])]})]});
            fillet(context, id + "F14", {"entities" : qUnion([Q0, Q1, Q2, Q3, Q4, Q5]), "radius" : 3 * mm, "tangentPropagation" : true, "allowEdgeOverflow" : false});
        }
        {
            var Q0;
            Q0=makeQuery(id+"F1.opExtrude","CAP_EDGE",EDGE,{"disambiguationData":[OSD([sQuery(id+"F0.wireOp",EDGE,"E1.bottom")])],"isStart":false});
            fillet(context, id + "F15", {"entities" : qUnion([Q0]), "radius" : 2 * mm, "tangentPropagation" : true, "allowEdgeOverflow" : false});
        }
        {
            var Q0;
            {var subQ0=sQuery(id+"F0.wireOp",EDGE,"E1.bottom");var subQ1=sQuery(id+"F0.wireOp",EDGE,"E1.top");var subQ2=sQuery(id+"F0.wireOp",EDGE,"E1.left");var subQ3=sQuery(id+"F0.wireOp",EDGE,"E1.right");var subQ4=sQuery(id+"F0.wireOp",EDGE,"E4");var subQ5=sQuery(id+"F0.wireOp",EDGE,"E5");var subQ6=sQuery(id+"F0.wireOp",EDGE,"E6");var subQ7=sQuery(id+"F0.wireOp",EDGE,"E7");var subQ8=sQuery(id+"F0.wireOp",EDGE,"E21.filletArc");var subQ9=sQuery(id+"F0.wireOp",EDGE,"E22.filletArc");var subQ10=sQuery(id+"F0.wireOp",EDGE,"E23.filletArc");var subQ11=sQuery(id+"F0.wireOp",EDGE,"E24.filletArc");Q0=makeQuery(id+"F2.boolean.opBoolean","SPLIT",FACE,{"disambiguationData":[TD([makeQuery(id+"F1.opExtrude","SWEPT_FACE",FACE,{"disambiguationData":[OSD([subQ0])]})])],"derivedFrom":makeQuery(id+"F1.opExtrude","CAP_FACE",FACE,{"disambiguationData":[OSD([subQ0,subQ1,subQ2,subQ3,subQ4,subQ5,subQ6,subQ7,subQ8,subQ9,subQ10,subQ11])],"isStart":true})});}
            var sketch = newSketch(context, id + "F16", { "sketchPlane" : qUnion([Q0])});
            skLineSegment(sketch, "E79", {"start": v(94.05, 208.38) * mm, "end": v(94.05, 238.38) * mm, "construction": true});
            skCircle(sketch, "E80", {"center": v(94.05, 238.38) * mm, "radius": 6 * mm});
            skArc(sketch, "E81", {"start": v(109.05, 238.38) * mm, "mid": v(94.05, 253.38) * mm, "end": v(79.05, 238.38) * mm});
            skLineSegment(sketch, "E82", {"start": v(79.05, 238.38) * mm, "end": v(79.05, 226.38) * mm});
            skLineSegment(sketch, "E83", {"start": v(109.05, 238.38) * mm, "end": v(109.05, 226.38) * mm});
            skLineSegment(sketch, "E84", {"start": v(79.05, 226.38) * mm, "end": v(61.05, 208.38) * mm});
            skLineSegment(sketch, "E85", {"start": v(109.05, 226.38) * mm, "end": v(127.05, 208.38) * mm});
            skLineSegment(sketch, "E86", {"start": v(14.05, 118.38) * mm, "end": v(174.05, 118.38) * mm, "construction": true});
            skLineSegment(sketch, "E87.MirrorCS", {"start": v(109.05, 10.38) * mm, "end": v(127.05, 28.38) * mm});
            skLineSegment(sketch, "E88.MirrorCS", {"start": v(79.05, 10.38) * mm, "end": v(61.05, 28.38) * mm});
            skLineSegment(sketch, "E89.MirrorCS", {"start": v(79.05, -1.62) * mm, "end": v(79.05, 10.38) * mm});
            skLineSegment(sketch, "E90.MirrorCS", {"start": v(109.05, -1.62) * mm, "end": v(109.05, 10.38) * mm});
            skArc(sketch, "E91.MirrorCS", {"start": v(109.05, -1.62) * mm, "mid": v(94.05, -16.62) * mm, "end": v(79.05, -1.62) * mm});
            skCircle(sketch, "E92.MirrorC", {"center": v(94.05, -1.62) * mm, "radius": 6 * mm});
            skSolve(sketch);
        }
        {
            var Q0;
            Q0=makeQuery(id+"F16.imprint","IMPRINT",FACE,{"disambiguationData":[TD([[makeQuery(id+"F16.imprint","IMPRINT",EDGE,{"derivedFrom":makeQuery(id+"F1.opExtrude","CAP_EDGE",EDGE,{"disambiguationData":[OSD([sQuery(id+"F0.wireOp",EDGE,"E1.left")])],"isStart":true})}),-1.0]])]});
            var Q1;
            Q1=makeQuery(id+"F16.imprint","IMPRINT",FACE,{"disambiguationData":[TD([[makeQuery(id+"F16.imprint","IMPRINT",EDGE,{"derivedFrom":sQuery(id+"F16.wireOp",EDGE,"E80")}),-1.0]])]});
            var Q2;
            {var subQ2=sQuery(id+"F16.wireOp",EDGE,"E87.MirrorCS");Q2=makeQuery(id+"F16.imprint","IMPRINT",FACE,{"disambiguationData":[TD([[makeQuery(id+"F16.imprint","IMPRINT",EDGE,{"derivedFrom":subQ2}),1.0]])]});}
            var Q3;
            {var subQ0=sQuery(id+"F4.wireOp",EDGE,"E36.filletArc");var subQ1=sQuery(id+"F4.wireOp",EDGE,"E35.filletArc");var subQ2=sQuery(id+"F4.wireOp",EDGE,"E34.filletArc");var subQ3=sQuery(id+"F4.wireOp",EDGE,"E33.filletArc");var subQ4=sQuery(id+"F4.wireOp",EDGE,"E27.0");var subQ5=sQuery(id+"F4.wireOp",EDGE,"E30");var subQ6=sQuery(id+"F4.wireOp",EDGE,"E28.0");var subQ7=sQuery(id+"F4.wireOp",EDGE,"E29");Q3=makeQuery(id+"F6.boolean.opBoolean","SPLIT",FACE,{"disambiguationData":[TD([makeQuery(id+"F5.opExtrude","SWEPT_FACE",FACE,{"disambiguationData":[OSD([subQ4])]})])],"derivedFrom":makeQuery(id+"F5.opExtrude","CAP_FACE",FACE,{"disambiguationData":[OSD([subQ4,subQ6,subQ7,subQ5,subQ3,subQ2,subQ1,subQ0,sQuery(id+"F4.wireOp",EDGE,"E41"),sQuery(id+"F4.wireOp",EDGE,"E42"),sQuery(id+"F4.wireOp",EDGE,"E43"),sQuery(id+"F4.wireOp",EDGE,"E45"),sQuery(id+"F4.wireOp",EDGE,"E46"),sQuery(id+"F4.wireOp",EDGE,"E47.filletArc"),sQuery(id+"F4.wireOp",EDGE,"E48.filletArc"),sQuery(id+"F4.wireOp",EDGE,"E49.filletArc"),sQuery(id+"F4.wireOp",EDGE,"E50.filletArc"),sQuery(id+"F4.wireOp",EDGE,"E51.filletArc"),sQuery(id+"F4.wireOp",EDGE,"E52.filletArc"),sQuery(id+"F4.wireOp",EDGE,"E53.0.MirrorCS"),sQuery(id+"F4.wireOp",EDGE,"E54.0.MirrorCS"),sQuery(id+"F4.wireOp",EDGE,"E55.0.MirrorCS"),sQuery(id+"F4.wireOp",EDGE,"E56.0.MirrorCS"),sQuery(id+"F4.wireOp",EDGE,"E57.0.MirrorCS"),sQuery(id+"F4.wireOp",EDGE,"E58.0.MirrorCS"),sQuery(id+"F4.wireOp",EDGE,"E59.0.MirrorCS"),sQuery(id+"F4.wireOp",EDGE,"E60.0.MirrorCS"),sQuery(id+"F4.wireOp",EDGE,"E61.0.MirrorCS"),sQuery(id+"F4.wireOp",EDGE,"E62.0.MirrorCS"),sQuery(id+"F4.wireOp",EDGE,"E63.0.MirrorCS")])],"isStart":true})});}
            extrude(context, id + "F17", {"entities" : qUnion([Q0, Q1, Q2]), "operationType" : NewBodyOperationType.ADD, "endBound" : BoundingType.UP_TO_SURFACE, "endBoundEntityFace" : qUnion([Q3]), "depth" : 25 * mm});
        }
    });
